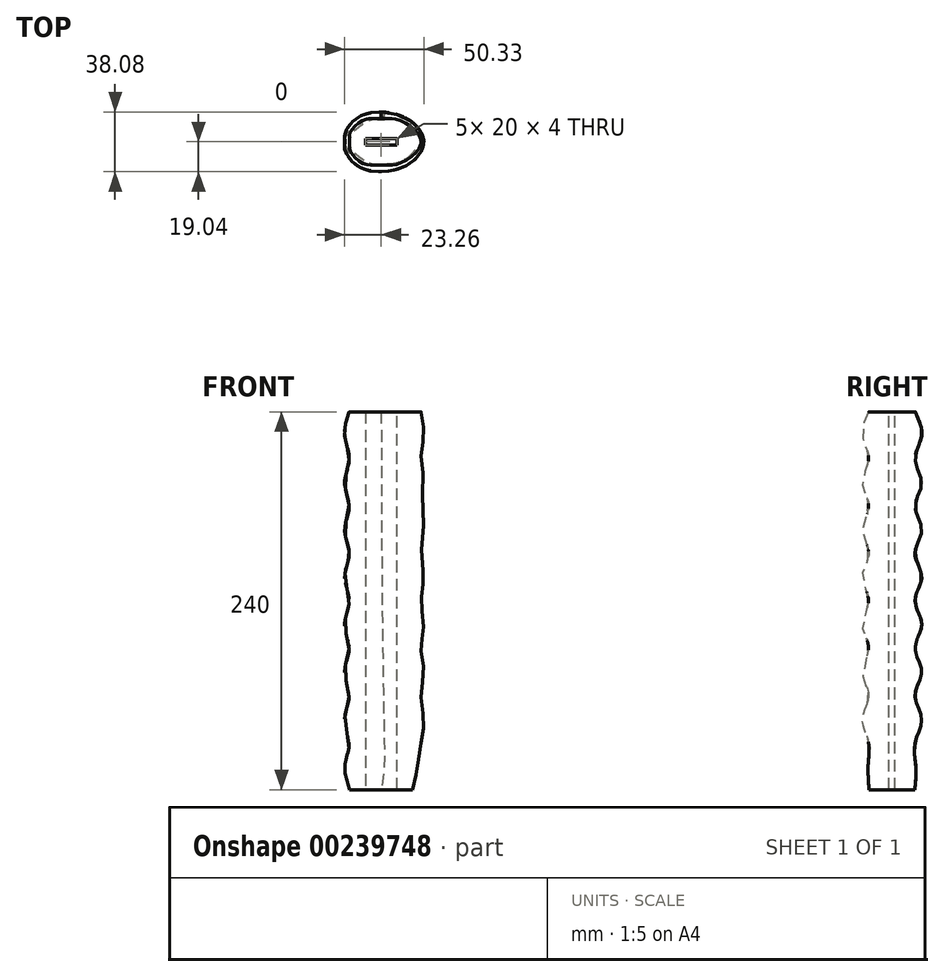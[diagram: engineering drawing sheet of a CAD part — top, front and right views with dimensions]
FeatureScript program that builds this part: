
annotation { "Feature Type Name" : "Feature", "Feature Type Description" : "" }
export const myFeature = defineFeature(function(context is Context, id is Id, definition is map)
    precondition{}
    {
        {
            assignVariable(context, id + "F0", {"name" : "d", "anyValue" : 15});
        }
        {
            var Q0;
            Q0=qCreatedBy(makeId("Top.planeOp"),FACE);
            var sketch = newSketch(context, id + "F1", { "sketchPlane" : qUnion([Q0])});
            skLineSegment(sketch, "E0.bottom", {"start": v(-10, -12.5) * mm, "end": v(10, -12.5) * mm, "construction": true});
            skLineSegment(sketch, "E0.top", {"start": v(-10, 12.5) * mm, "end": v(10, 12.5) * mm, "construction": true});
            skLineSegment(sketch, "E0.left", {"start": v(-10, -12.5) * mm, "end": v(-10, 12.5) * mm, "construction": true});
            skLineSegment(sketch, "E0.right", {"start": v(10, -12.5) * mm, "end": v(10, 12.5) * mm, "construction": true});
            skPoint(sketch, "E0.middle", {"position": v(0, 0) * mm});
            skLineSegment(sketch, "E1", {"start": v(-10, 0) * mm, "end": v(-20, 0) * mm, "construction": true});
            skPoint(sketch, "E1.endSnap0", {"position": v(-10, 0) * mm});
            skLineSegment(sketch, "E2", {"start": v(10, 0) * mm, "end": v(20, 0) * mm, "construction": true});
            skPoint(sketch, "E2.endSnap0", {"position": v(10, 0) * mm});
            skLineSegment(sketch, "E3", {"start": v(0, 12.5) * mm, "end": v(0, 14.5) * mm});
            skPoint(sketch, "E3.endSnap0", {"position": v(0, 12.5) * mm});
            skLineSegment(sketch, "E4", {"start": v(0, -12.5) * mm, "end": v(0, -14.5) * mm});
            skPoint(sketch, "E4.endSnap0", {"position": v(0, -12.5) * mm});
            skFitSpline(sketch, "E5", {"points": [v(-20, 0) * mm, v(-10, 12.5) * mm, v(0, 14.5) * mm, v(10, 12.5) * mm, v(20, 0) * mm, v(10, -12.5) * mm, v(0, -14.5) * mm, v(-10, -12.5) * mm, v(-20, 0) * mm]});
            skSolve(sketch);
        }
        {
            var Q0;
            Q0=qCreatedBy(makeId("Top.planeOp"),FACE);
            cPlane(context, id + "F2", {"entities" : qUnion([Q0]), "cplaneType" : CPlaneType.OFFSET, "offset" : (1 * getVariable(context, 'd')) * mm, "width" : 150 * mm, "height" : 150 * mm});
        }
        {
            var Q0;
            Q0=qCreatedBy(id+"F2.planeOp",FACE);
            var sketch = newSketch(context, id + "F3", { "sketchPlane" : qUnion([Q0])});
            skLineSegment(sketch, "E6.bottom", {"start": v(-13, 12.5) * mm, "end": v(13, 12.5) * mm, "construction": true});
            skLineSegment(sketch, "E6.top", {"start": v(-13, -12.5) * mm, "end": v(13, -12.5) * mm, "construction": true});
            skLineSegment(sketch, "E6.left", {"start": v(-13, 12.5) * mm, "end": v(-13, -12.5) * mm, "construction": true});
            skLineSegment(sketch, "E6.right", {"start": v(13, 12.5) * mm, "end": v(13, -12.5) * mm, "construction": true});
            skPoint(sketch, "E6.middle", {"position": v(0, 0) * mm});
            skLineSegment(sketch, "E7", {"start": v(-13, 0) * mm, "end": v(-23, 0) * mm, "construction": true});
            skPoint(sketch, "E7.endSnap0", {"position": v(-13, 0) * mm});
            skLineSegment(sketch, "E8", {"start": v(13, 0) * mm, "end": v(23, 0) * mm, "construction": true});
            skPoint(sketch, "E8.endSnap0", {"position": v(13, 0) * mm});
            skFitSpline(sketch, "E9", {"points": [v(-23, 0) * mm, v(-13, 12.5) * mm, v(13, 12.5) * mm, v(23, 0) * mm, v(13, -12.5) * mm, v(-13, -12.5) * mm, v(-23, 0) * mm]});
            skSolve(sketch);
        }
        {
            var Q0;
            Q0=qCreatedBy(makeId("Top.planeOp"),FACE);
            cPlane(context, id + "F4", {"entities" : qUnion([Q0]), "cplaneType" : CPlaneType.OFFSET, "offset" : (2 * getVariable(context, 'd')) * mm, "width" : 150 * mm, "height" : 150 * mm});
        }
        {
            var Q0;
            Q0=qCreatedBy(makeId("Top.planeOp"),FACE);
            cPlane(context, id + "F5", {"entities" : qUnion([Q0]), "cplaneType" : CPlaneType.OFFSET, "offset" : (3 * getVariable(context, 'd')) * mm, "width" : 150 * mm, "height" : 150 * mm});
        }
        {
            var Q0;
            Q0=qCreatedBy(makeId("Top.planeOp"),FACE);
            cPlane(context, id + "F6", {"entities" : qUnion([Q0]), "cplaneType" : CPlaneType.OFFSET, "offset" : 60 * mm, "width" : 150 * mm, "height" : 150 * mm});
        }
        {
            var Q0;
            Q0=qCreatedBy(makeId("Top.planeOp"),FACE);
            cPlane(context, id + "F7", {"entities" : qUnion([Q0]), "cplaneType" : CPlaneType.OFFSET, "offset" : 75 * mm, "width" : 150 * mm, "height" : 150 * mm});
        }
        {
            var Q0;
            Q0=qCreatedBy(makeId("Top.planeOp"),FACE);
            cPlane(context, id + "F8", {"entities" : qUnion([Q0]), "cplaneType" : CPlaneType.OFFSET, "offset" : 6 * getVariable(context, 'd') * mm, "width" : 150 * mm, "height" : 150 * mm});
        }
        {
            var Q0;
            Q0=qCreatedBy(makeId("Top.planeOp"),FACE);
            cPlane(context, id + "F9", {"entities" : qUnion([Q0]), "cplaneType" : CPlaneType.OFFSET, "offset" : (7 * getVariable(context, 'd')) * mm, "width" : 150 * mm, "height" : 150 * mm});
        }
        {
            var Q0;
            Q0=qCreatedBy(makeId("Top.planeOp"),FACE);
            cPlane(context, id + "F10", {"entities" : qUnion([Q0]), "cplaneType" : CPlaneType.OFFSET, "offset" : (8 * getVariable(context, 'd')) * mm, "width" : 150 * mm, "height" : 150 * mm});
        }
        {
            var Q0;
            Q0=qCreatedBy(makeId("Top.planeOp"),FACE);
            cPlane(context, id + "F11", {"entities" : qUnion([Q0]), "cplaneType" : CPlaneType.OFFSET, "offset" : (9 * getVariable(context, 'd')) * mm, "width" : 150 * mm, "height" : 150 * mm});
        }
        {
            var Q0;
            Q0=qCreatedBy(makeId("Top.planeOp"),FACE);
            cPlane(context, id + "F12", {"entities" : qUnion([Q0]), "cplaneType" : CPlaneType.OFFSET, "offset" : (10 * getVariable(context, 'd')) * mm, "width" : 150 * mm, "height" : 150 * mm});
        }
        {
            var Q0;
            Q0=qCreatedBy(makeId("Top.planeOp"),FACE);
            cPlane(context, id + "F13", {"entities" : qUnion([Q0]), "cplaneType" : CPlaneType.OFFSET, "offset" : (11 * getVariable(context, 'd')) * mm, "width" : 150 * mm, "height" : 150 * mm});
        }
        {
            var Q0;
            Q0=qCreatedBy(makeId("Top.planeOp"),FACE);
            cPlane(context, id + "F14", {"entities" : qUnion([Q0]), "cplaneType" : CPlaneType.OFFSET, "offset" : (12 * getVariable(context, 'd')) * mm, "width" : 150 * mm, "height" : 150 * mm});
        }
        {
            var Q0;
            Q0=qCreatedBy(makeId("Top.planeOp"),FACE);
            cPlane(context, id + "F15", {"entities" : qUnion([Q0]), "cplaneType" : CPlaneType.OFFSET, "offset" : (13 * getVariable(context, 'd')) * mm, "width" : 150 * mm, "height" : 150 * mm});
        }
        {
            var Q0;
            Q0=qCreatedBy(makeId("Top.planeOp"),FACE);
            cPlane(context, id + "F16", {"entities" : qUnion([Q0]), "cplaneType" : CPlaneType.OFFSET, "offset" : (14 * getVariable(context, 'd')) * mm, "width" : 150 * mm, "height" : 150 * mm});
        }
        {
            var Q0;
            Q0=qCreatedBy(makeId("Top.planeOp"),FACE);
            cPlane(context, id + "F17", {"entities" : qUnion([Q0]), "cplaneType" : CPlaneType.OFFSET, "offset" : (15 * getVariable(context, 'd')) * mm, "width" : 150 * mm, "height" : 150 * mm});
        }
        {
            var Q0;
            Q0=qCreatedBy(makeId("Top.planeOp"),FACE);
            cPlane(context, id + "F18", {"entities" : qUnion([Q0]), "cplaneType" : CPlaneType.OFFSET, "offset" : (16 * getVariable(context, 'd')) * mm, "width" : 150 * mm, "height" : 150 * mm});
        }
        {
            var Q0;
            Q0=qCreatedBy(id+"F4.planeOp",FACE);
            var sketch = newSketch(context, id + "F19", { "sketchPlane" : qUnion([Q0])});
            skFitSpline(sketch, "E10.0", {"points": [v(-20, 0) * mm, v(-20, 5.08) * mm, v(-10.3, 14.2) * mm, v(0, 14.63) * mm, v(10.3, 14.2) * mm, v(25.4, 0) * mm, v(10.3, -14.2) * mm, v(0, -14.63) * mm, v(-10.3, -14.2) * mm, v(-20, -5.08) * mm, v(-20, 0) * mm]});
            skSolve(sketch);
        }
        {
            var Q0;
            Q0=qCreatedBy(id+"F5.planeOp",FACE);
            var sketch = newSketch(context, id + "F20", { "sketchPlane" : qUnion([Q0])});
            skFitSpline(sketch, "E11.0", {"points": [v(-23, 0) * mm, v(-23, 4.88) * mm, v(-13.84, 15.99) * mm, v(13.84, 15.99) * mm, v(27.03, 0) * mm, v(13.84, -15.99) * mm, v(-13.84, -15.99) * mm, v(-23, -4.88) * mm, v(-23, 0) * mm]});
            skSolve(sketch);
        }
        {
            var Q0;
            Q0=qCreatedBy(id+"F6.planeOp",FACE);
            var sketch = newSketch(context, id + "F21", { "sketchPlane" : qUnion([Q0])});
            skFitSpline(sketch, "E12.0", {"points": [v(-20, 0) * mm, v(-20, 5.08) * mm, v(-10.3, 14.2) * mm, v(0, 14.63) * mm, v(10.3, 14.2) * mm, v(25.4, 0) * mm, v(10.3, -14.2) * mm, v(0, -14.63) * mm, v(-10.3, -14.2) * mm, v(-20, -5.08) * mm, v(-20, 0) * mm]});
            skSolve(sketch);
        }
        {
            var Q0;
            Q0=qCreatedBy(id+"F7.planeOp",FACE);
            var sketch = newSketch(context, id + "F22", { "sketchPlane" : qUnion([Q0])});
            skFitSpline(sketch, "E13.0", {"points": [v(-23, 0) * mm, v(-23, 4.88) * mm, v(-13.84, 15.99) * mm, v(13.84, 15.99) * mm, v(27.03, 0) * mm, v(13.84, -15.99) * mm, v(-13.84, -15.99) * mm, v(-23, -4.88) * mm, v(-23, 0) * mm]});
            skSolve(sketch);
        }
        {
            var Q0;
            Q0=qCreatedBy(id+"F8.planeOp",FACE);
            var sketch = newSketch(context, id + "F23", { "sketchPlane" : qUnion([Q0])});
            skFitSpline(sketch, "E14.0", {"points": [v(-20, 0) * mm, v(-20, 5.08) * mm, v(-10.3, 14.2) * mm, v(0, 14.63) * mm, v(10.3, 14.2) * mm, v(25.4, 0) * mm, v(10.3, -14.2) * mm, v(0, -14.63) * mm, v(-10.3, -14.2) * mm, v(-20, -5.08) * mm, v(-20, 0) * mm]});
            skSolve(sketch);
        }
        {
            var Q0;
            Q0=qCreatedBy(id+"F9.planeOp",FACE);
            var sketch = newSketch(context, id + "F24", { "sketchPlane" : qUnion([Q0])});
            skFitSpline(sketch, "E15.0", {"points": [v(-23, 0) * mm, v(-23, 4.88) * mm, v(-13.84, 15.99) * mm, v(13.84, 15.99) * mm, v(27.03, 0) * mm, v(13.84, -15.99) * mm, v(-13.84, -15.99) * mm, v(-23, -4.88) * mm, v(-23, 0) * mm]});
            skSolve(sketch);
        }
        {
            var Q0;
            Q0=qCreatedBy(id+"F10.planeOp",FACE);
            var sketch = newSketch(context, id + "F25", { "sketchPlane" : qUnion([Q0])});
            skFitSpline(sketch, "E16.0", {"points": [v(-20, 0) * mm, v(-20, 5.08) * mm, v(-10.3, 14.2) * mm, v(0, 14.63) * mm, v(10.3, 14.2) * mm, v(25.4, 0) * mm, v(10.3, -14.2) * mm, v(0, -14.63) * mm, v(-10.3, -14.2) * mm, v(-20, -5.08) * mm, v(-20, 0) * mm]});
            skSolve(sketch);
        }
        {
            var Q0;
            Q0=qCreatedBy(id+"F11.planeOp",FACE);
            var sketch = newSketch(context, id + "F26", { "sketchPlane" : qUnion([Q0])});
            skFitSpline(sketch, "E17.0", {"points": [v(-23, 0) * mm, v(-23, 4.88) * mm, v(-13.84, 15.99) * mm, v(13.84, 15.99) * mm, v(27.03, 0) * mm, v(13.84, -15.99) * mm, v(-13.84, -15.99) * mm, v(-23, -4.88) * mm, v(-23, 0) * mm]});
            skSolve(sketch);
        }
        {
            var Q0;
            Q0=qCreatedBy(id+"F12.planeOp",FACE);
            var sketch = newSketch(context, id + "F27", { "sketchPlane" : qUnion([Q0])});
            skFitSpline(sketch, "E18.0", {"points": [v(-20, 0) * mm, v(-20, 5.08) * mm, v(-10.3, 14.2) * mm, v(0, 14.63) * mm, v(10.3, 14.2) * mm, v(25.4, 0) * mm, v(10.3, -14.2) * mm, v(0, -14.63) * mm, v(-10.3, -14.2) * mm, v(-20, -5.08) * mm, v(-20, 0) * mm]});
            skSolve(sketch);
        }
        {
            var Q0;
            Q0=qCreatedBy(id+"F13.planeOp",FACE);
            var sketch = newSketch(context, id + "F28", { "sketchPlane" : qUnion([Q0])});
            skFitSpline(sketch, "E19.0", {"points": [v(-23, 0) * mm, v(-23, 4.88) * mm, v(-13.84, 15.99) * mm, v(13.84, 15.99) * mm, v(27.03, 0) * mm, v(13.84, -15.99) * mm, v(-13.84, -15.99) * mm, v(-23, -4.88) * mm, v(-23, 0) * mm]});
            skSolve(sketch);
        }
        {
            var Q0;
            Q0=qCreatedBy(id+"F14.planeOp",FACE);
            var sketch = newSketch(context, id + "F29", { "sketchPlane" : qUnion([Q0])});
            skFitSpline(sketch, "E20.0", {"points": [v(-20, 0) * mm, v(-20, 5.08) * mm, v(-10.3, 14.2) * mm, v(0, 14.63) * mm, v(10.3, 14.2) * mm, v(25.4, 0) * mm, v(10.3, -14.2) * mm, v(0, -14.63) * mm, v(-10.3, -14.2) * mm, v(-20, -5.08) * mm, v(-20, 0) * mm]});
            skSolve(sketch);
        }
        {
            var Q0;
            Q0=qCreatedBy(id+"F15.planeOp",FACE);
            var sketch = newSketch(context, id + "F30", { "sketchPlane" : qUnion([Q0])});
            skFitSpline(sketch, "E21.0", {"points": [v(-23, 0) * mm, v(-23, 4.88) * mm, v(-13.84, 15.99) * mm, v(13.84, 15.99) * mm, v(27.03, 0) * mm, v(13.84, -15.99) * mm, v(-13.84, -15.99) * mm, v(-23, -4.88) * mm, v(-23, 0) * mm]});
            skSolve(sketch);
        }
        {
            var Q0;
            Q0=qCreatedBy(id+"F16.planeOp",FACE);
            var sketch = newSketch(context, id + "F31", { "sketchPlane" : qUnion([Q0])});
            skFitSpline(sketch, "E22.0", {"points": [v(-20, 0) * mm, v(-20, 5.08) * mm, v(-10.3, 14.2) * mm, v(0, 14.63) * mm, v(10.3, 14.2) * mm, v(25.4, 0) * mm, v(10.3, -14.2) * mm, v(0, -14.63) * mm, v(-10.3, -14.2) * mm, v(-20, -5.08) * mm, v(-20, 0) * mm]});
            skSolve(sketch);
        }
        {
            var Q0;
            Q0=qCreatedBy(id+"F17.planeOp",FACE);
            var sketch = newSketch(context, id + "F32", { "sketchPlane" : qUnion([Q0])});
            skFitSpline(sketch, "E23.0", {"points": [v(-23, 0) * mm, v(-23, 4.88) * mm, v(-13.84, 15.99) * mm, v(13.84, 15.99) * mm, v(27.03, 0) * mm, v(13.84, -15.99) * mm, v(-13.84, -15.99) * mm, v(-23, -4.88) * mm, v(-23, 0) * mm]});
            skSolve(sketch);
        }
        {
            var Q0;
            Q0=qCreatedBy(id+"F18.planeOp",FACE);
            var sketch = newSketch(context, id + "F33", { "sketchPlane" : qUnion([Q0])});
            skFitSpline(sketch, "E24.0", {"points": [v(-20, 0) * mm, v(-20, 5.08) * mm, v(-10.3, 14.2) * mm, v(0, 14.63) * mm, v(10.3, 14.2) * mm, v(25.4, 0) * mm, v(10.3, -14.2) * mm, v(0, -14.63) * mm, v(-10.3, -14.2) * mm, v(-20, -5.08) * mm, v(-20, 0) * mm]});
            skSolve(sketch);
        }
        {
            var Q0;
            Q0=qCreatedBy(makeId("Front.planeOp"),FACE);
            var sketch = newSketch(context, id + "F34", { "sketchPlane" : qUnion([Q0])});
            skPoint(sketch, "E25.0", {"position": v(20, 0) * mm});
            skPoint(sketch, "E26.0", {"position": v(23, 15) * mm});
            skLineSegment(sketch, "E27.0", {"start": v(-20, 30) * mm, "end": v(20, 30) * mm, "construction": true});
            skLineSegment(sketch, "E28.0", {"start": v(-23, 45) * mm, "end": v(23, 45) * mm, "construction": true});
            skLineSegment(sketch, "E29.0", {"start": v(-20, 60) * mm, "end": v(20, 60) * mm, "construction": true});
            skLineSegment(sketch, "E30.0", {"start": v(-23, 75) * mm, "end": v(23, 75) * mm, "construction": true});
            skLineSegment(sketch, "E31.0", {"start": v(-20, 90) * mm, "end": v(20, 90) * mm, "construction": true});
            skLineSegment(sketch, "E32.0", {"start": v(-23, 105) * mm, "end": v(23, 105) * mm, "construction": true});
            skLineSegment(sketch, "E33.0", {"start": v(-20, 120) * mm, "end": v(20, 120) * mm, "construction": true});
            skLineSegment(sketch, "E34.0", {"start": v(-23, 135) * mm, "end": v(23, 135) * mm, "construction": true});
            skLineSegment(sketch, "E35.0", {"start": v(-20, 150) * mm, "end": v(20, 150) * mm, "construction": true});
            skLineSegment(sketch, "E36.0", {"start": v(-23, 165) * mm, "end": v(23, 165) * mm, "construction": true});
            skLineSegment(sketch, "E37.0", {"start": v(-20, 180) * mm, "end": v(20, 180) * mm, "construction": true});
            skLineSegment(sketch, "E38.0", {"start": v(-23, 195) * mm, "end": v(23, 195) * mm, "construction": true});
            skLineSegment(sketch, "E39.0", {"start": v(-20, 210) * mm, "end": v(20, 210) * mm, "construction": true});
            skLineSegment(sketch, "E40.0", {"start": v(-23, 225) * mm, "end": v(23, 225) * mm, "construction": true});
            skLineSegment(sketch, "E41.0", {"start": v(-20, 240) * mm, "end": v(20, 240) * mm, "construction": true});
            skArc(sketch, "E42", {"start": v(21.5, 7.5) * mm, "mid": v(20.38, 3.82) * mm, "end": v(20, 0) * mm});
            skArc(sketch, "E43", {"start": v(21.5, 7.5) * mm, "mid": v(23, 15) * mm, "end": v(21.5, 22.5) * mm});
            skArc(sketch, "E44", {"start": v(21.5, 37.5) * mm, "mid": v(20, 30) * mm, "end": v(21.5, 22.5) * mm});
            skArc(sketch, "E45", {"start": v(21.5, 37.5) * mm, "mid": v(23, 45) * mm, "end": v(21.5, 52.5) * mm});
            skArc(sketch, "E46", {"start": v(21.5, 67.5) * mm, "mid": v(20, 60) * mm, "end": v(21.5, 52.5) * mm});
            skArc(sketch, "E47", {"start": v(21.5, 67.5) * mm, "mid": v(23, 75) * mm, "end": v(21.5, 82.5) * mm});
            skArc(sketch, "E48", {"start": v(21.5, 97.5) * mm, "mid": v(20, 90) * mm, "end": v(21.5, 82.5) * mm});
            skArc(sketch, "E49", {"start": v(21.5, 97.5) * mm, "mid": v(23, 105) * mm, "end": v(21.5, 112.5) * mm});
            skArc(sketch, "E50", {"start": v(21.5, 127.5) * mm, "mid": v(20, 120) * mm, "end": v(21.5, 112.5) * mm});
            skArc(sketch, "E51", {"start": v(21.5, 127.5) * mm, "mid": v(23, 135) * mm, "end": v(21.5, 142.5) * mm});
            skArc(sketch, "E52", {"start": v(21.5, 157.5) * mm, "mid": v(20, 150) * mm, "end": v(21.5, 142.5) * mm});
            skArc(sketch, "E53", {"start": v(21.5, 157.5) * mm, "mid": v(23, 165) * mm, "end": v(21.5, 172.5) * mm});
            skArc(sketch, "E54", {"start": v(21.5, 187.5) * mm, "mid": v(20, 180) * mm, "end": v(21.5, 172.5) * mm});
            skArc(sketch, "E55", {"start": v(21.5, 187.5) * mm, "mid": v(23, 195) * mm, "end": v(21.5, 202.5) * mm});
            skArc(sketch, "E56", {"start": v(21.5, 217.5) * mm, "mid": v(20, 210) * mm, "end": v(21.5, 202.5) * mm});
            skArc(sketch, "E57", {"start": v(21.5, 217.5) * mm, "mid": v(23, 225) * mm, "end": v(21.5, 232.5) * mm});
            skArc(sketch, "E58", {"start": v(20, 240) * mm, "mid": v(20.38, 236.18) * mm, "end": v(21.5, 232.5) * mm});
            skLineSegment(sketch, "E59", {"start": v(0, -67.93) * mm, "end": v(0, 364.44) * mm, "construction": true});
            skArc(sketch, "E60.MirrorCS", {"start": v(-21.5, 7.5) * mm, "mid": v(-20.38, 3.82) * mm, "end": v(-20, 0) * mm});
            skArc(sketch, "E61.MirrorCS", {"start": v(-20, 240) * mm, "mid": v(-20.38, 236.18) * mm, "end": v(-21.5, 232.5) * mm});
            skArc(sketch, "E62.MirrorCS", {"start": v(-21.5, 97.5) * mm, "mid": v(-23, 105) * mm, "end": v(-21.5, 112.5) * mm});
            skArc(sketch, "E63.MirrorCS", {"start": v(-21.5, 127.5) * mm, "mid": v(-23, 135) * mm, "end": v(-21.5, 142.5) * mm});
            skArc(sketch, "E64.MirrorCS", {"start": v(-21.5, 67.5) * mm, "mid": v(-23, 75) * mm, "end": v(-21.5, 82.5) * mm});
            skArc(sketch, "E65.MirrorCS", {"start": v(-21.5, 127.5) * mm, "mid": v(-20, 120) * mm, "end": v(-21.5, 112.5) * mm});
            skArc(sketch, "E66.MirrorCS", {"start": v(-21.5, 157.5) * mm, "mid": v(-23, 165) * mm, "end": v(-21.5, 172.5) * mm});
            skArc(sketch, "E67.MirrorCS", {"start": v(-21.5, 187.5) * mm, "mid": v(-23, 195) * mm, "end": v(-21.5, 202.5) * mm});
            skArc(sketch, "E68.MirrorCS", {"start": v(-21.5, 97.5) * mm, "mid": v(-20, 90) * mm, "end": v(-21.5, 82.5) * mm});
            skArc(sketch, "E69.MirrorCS", {"start": v(-21.5, 37.5) * mm, "mid": v(-23, 45) * mm, "end": v(-21.5, 52.5) * mm});
            skArc(sketch, "E70.MirrorCS", {"start": v(-21.5, 67.5) * mm, "mid": v(-20, 60) * mm, "end": v(-21.5, 52.5) * mm});
            skArc(sketch, "E71.MirrorCS", {"start": v(-21.5, 217.5) * mm, "mid": v(-23, 225) * mm, "end": v(-21.5, 232.5) * mm});
            skArc(sketch, "E72.MirrorCS", {"start": v(-21.5, 37.5) * mm, "mid": v(-20, 30) * mm, "end": v(-21.5, 22.5) * mm});
            skArc(sketch, "E73.MirrorCS", {"start": v(-21.5, 187.5) * mm, "mid": v(-20, 180) * mm, "end": v(-21.5, 172.5) * mm});
            skArc(sketch, "E74.MirrorCS", {"start": v(-21.5, 157.5) * mm, "mid": v(-20, 150) * mm, "end": v(-21.5, 142.5) * mm});
            skArc(sketch, "E75.MirrorCS", {"start": v(-21.5, 7.5) * mm, "mid": v(-23, 15) * mm, "end": v(-21.5, 22.5) * mm});
            skArc(sketch, "E76.MirrorCS", {"start": v(-21.5, 217.5) * mm, "mid": v(-20, 210) * mm, "end": v(-21.5, 202.5) * mm});
            skPoint(sketch, "E77.MirrorP", {"position": v(-23, 15) * mm});
            skPoint(sketch, "E78.MirrorP", {"position": v(-20, 0) * mm});
            skLineSegment(sketch, "E79", {"start": v(0, 0) * mm, "end": v(10, 0) * mm});
            skLineSegment(sketch, "E80", {"start": v(10, 0) * mm, "end": v(10, 240) * mm});
            skLineSegment(sketch, "E81", {"start": v(10, 240) * mm, "end": v(-10, 240) * mm});
            skLineSegment(sketch, "E82", {"start": v(-10, 240) * mm, "end": v(-10, 0) * mm});
            skLineSegment(sketch, "E83", {"start": v(-10, 0) * mm, "end": v(0, 0) * mm});
            skLineSegment(sketch, "E84", {"start": v(10, 0) * mm, "end": v(20, 0) * mm});
            skLineSegment(sketch, "E85", {"start": v(-10, 0) * mm, "end": v(-20, 0) * mm});
            skLineSegment(sketch, "E86", {"start": v(10, 240) * mm, "end": v(20, 240) * mm});
            skLineSegment(sketch, "E87", {"start": v(-10, 240) * mm, "end": v(-20, 240) * mm});
            skSolve(sketch);
        }
        {
            var Q0;
            Q0=makeQuery(id+"F33.imprint","IMPRINT",FACE,{"disambiguationData":[TD([[makeQuery(id+"F33.imprint","IMPRINT",EDGE,{"derivedFrom":sQuery(id+"F33.wireOp",EDGE,"E24.0")}),-1.0]])]});
            var Q1;
            Q1=makeQuery(id+"F32.imprint","IMPRINT",FACE,{"disambiguationData":[TD([[makeQuery(id+"F32.imprint","IMPRINT",EDGE,{"derivedFrom":sQuery(id+"F32.wireOp",EDGE,"E23.0")}),-1.0]])]});
            var Q2;
            Q2=makeQuery(id+"F31.imprint","IMPRINT",FACE,{"disambiguationData":[TD([[makeQuery(id+"F31.imprint","IMPRINT",EDGE,{"derivedFrom":sQuery(id+"F31.wireOp",EDGE,"E22.0")}),-1.0]])]});
            var Q3;
            Q3=makeQuery(id+"F30.imprint","IMPRINT",FACE,{"disambiguationData":[TD([[makeQuery(id+"F30.imprint","IMPRINT",EDGE,{"derivedFrom":sQuery(id+"F30.wireOp",EDGE,"E21.0")}),-1.0]])]});
            var Q4;
            Q4=makeQuery(id+"F29.imprint","IMPRINT",FACE,{"disambiguationData":[TD([[makeQuery(id+"F29.imprint","IMPRINT",EDGE,{"derivedFrom":sQuery(id+"F29.wireOp",EDGE,"E20.0")}),-1.0]])]});
            var Q5;
            Q5=makeQuery(id+"F28.imprint","IMPRINT",FACE,{"disambiguationData":[TD([[makeQuery(id+"F28.imprint","IMPRINT",EDGE,{"derivedFrom":sQuery(id+"F28.wireOp",EDGE,"E19.0")}),-1.0]])]});
            var Q6;
            Q6=makeQuery(id+"F27.imprint","IMPRINT",FACE,{"disambiguationData":[TD([[makeQuery(id+"F27.imprint","IMPRINT",EDGE,{"derivedFrom":sQuery(id+"F27.wireOp",EDGE,"E18.0")}),-1.0]])]});
            var Q7;
            Q7=makeQuery(id+"F26.imprint","IMPRINT",FACE,{"disambiguationData":[TD([[makeQuery(id+"F26.imprint","IMPRINT",EDGE,{"derivedFrom":sQuery(id+"F26.wireOp",EDGE,"E17.0")}),-1.0]])]});
            var Q8;
            Q8=makeQuery(id+"F25.imprint","IMPRINT",FACE,{"disambiguationData":[TD([[makeQuery(id+"F25.imprint","IMPRINT",EDGE,{"derivedFrom":sQuery(id+"F25.wireOp",EDGE,"E16.0")}),-1.0]])]});
            var Q9;
            Q9=makeQuery(id+"F24.imprint","IMPRINT",FACE,{"disambiguationData":[TD([[makeQuery(id+"F24.imprint","IMPRINT",EDGE,{"derivedFrom":sQuery(id+"F24.wireOp",EDGE,"E15.0")}),-1.0]])]});
            var Q10;
            Q10=makeQuery(id+"F23.imprint","IMPRINT",FACE,{"disambiguationData":[TD([[makeQuery(id+"F23.imprint","IMPRINT",EDGE,{"derivedFrom":sQuery(id+"F23.wireOp",EDGE,"E14.0")}),-1.0]])]});
            var Q11;
            Q11=makeQuery(id+"F22.imprint","IMPRINT",FACE,{"disambiguationData":[TD([[makeQuery(id+"F22.imprint","IMPRINT",EDGE,{"derivedFrom":sQuery(id+"F22.wireOp",EDGE,"E13.0")}),-1.0]])]});
            var Q12;
            Q12=makeQuery(id+"F21.imprint","IMPRINT",FACE,{"disambiguationData":[TD([[makeQuery(id+"F21.imprint","IMPRINT",EDGE,{"derivedFrom":sQuery(id+"F21.wireOp",EDGE,"E12.0")}),-1.0]])]});
            var Q13;
            Q13=makeQuery(id+"F20.imprint","IMPRINT",FACE,{"disambiguationData":[TD([[makeQuery(id+"F20.imprint","IMPRINT",EDGE,{"derivedFrom":sQuery(id+"F20.wireOp",EDGE,"E11.0")}),-1.0]])]});
            var Q14;
            Q14=makeQuery(id+"F19.imprint","IMPRINT",FACE,{"disambiguationData":[TD([[makeQuery(id+"F19.imprint","IMPRINT",EDGE,{"derivedFrom":sQuery(id+"F19.wireOp",EDGE,"E10.0")}),-1.0]])]});
            var Q15;
            Q15=makeQuery(id+"F3.imprint","IMPRINT",FACE,{"disambiguationData":[TD([[makeQuery(id+"F3.imprint","IMPRINT",EDGE,{"derivedFrom":sQuery(id+"F3.wireOp",EDGE,"E9")}),-1.0]])]});
            var Q16;
            {var subQ0=sQuery(id+"F1.wireOp",EDGE,"E5");var subQ1=makeQuery(id+"F1.imprint","IMPRINT",VERTEX,{"disambiguationData":[OD(0.0)],"derivedFrom":subQ0});Q16=makeQuery(id+"F1.imprint","IMPRINT",FACE,{"disambiguationData":[TD([[makeQuery(id+"F1.imprint","IMPRINT",EDGE,{"disambiguationData":[TD([[subQ1,-1.0]])],"derivedFrom":subQ0}),-1.0]])]});}
            loft(context, id + "F35", {"sheetProfilesArray" : [{ "sheetProfileEntities" : qUnion([Q0]) }, { "sheetProfileEntities" : qUnion([Q1]) }, { "sheetProfileEntities" : qUnion([Q2]) }, { "sheetProfileEntities" : qUnion([Q3]) }, { "sheetProfileEntities" : qUnion([Q4]) }, { "sheetProfileEntities" : qUnion([Q5]) }, { "sheetProfileEntities" : qUnion([Q6]) }, { "sheetProfileEntities" : qUnion([Q7]) }, { "sheetProfileEntities" : qUnion([Q8]) }, { "sheetProfileEntities" : qUnion([Q9]) }, { "sheetProfileEntities" : qUnion([Q10]) }, { "sheetProfileEntities" : qUnion([Q11]) }, { "sheetProfileEntities" : qUnion([Q12]) }, { "sheetProfileEntities" : qUnion([Q13]) }, { "sheetProfileEntities" : qUnion([Q14]) }, { "sheetProfileEntities" : qUnion([Q15]) }, { "sheetProfileEntities" : qUnion([Q16]) }]});
        }
        {
            var Q0;
            Q0=makeQuery(id+"F34.imprint","IMPRINT",FACE,{"disambiguationData":[TD([[makeQuery(id+"F34.imprint","IMPRINT",EDGE,{"derivedFrom":sQuery(id+"F34.wireOp",EDGE,"E79")}),1.0]])]});
            extrude(context, id + "F36", {"entities" : qUnion([Q0]), "operationType" : NewBodyOperationType.REMOVE, "oppositeDirection" : true, "depth" : 4 * mm, "symmetric" : true});
        }
    });
